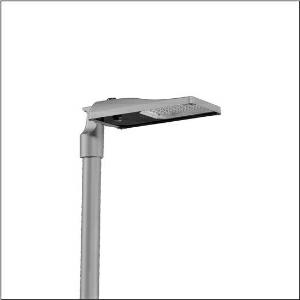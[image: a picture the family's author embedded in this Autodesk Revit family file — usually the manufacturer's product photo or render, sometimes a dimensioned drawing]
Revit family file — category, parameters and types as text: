
# Revit family: streetlight_sl_31_mini___st1_0a_5xh2d31t08ja_3c6a
name_source: partatom
category: Lighting Fixtures
units: mm (PartAtom-declared; Revit-internal decimal feet)

## family parameters
Cut with Voids When Loaded = No
Host = Face
Light Source = No
Part Type = Normal
Room Calculation Point = No
Round Connector Dimension = Use Diameter
Shared = No

## types (1)
- --- (1 x LED, 12270 lm, 82.5 W, 3000K)
    Apparent Load = 83 VA
    CIE Flux Codes = 40 73 97 100 100
    Color Rendering = 70
    Color Temperature = 3000K
    Default Elevation = 1800 mm
    Description = Streetlight SL 31 mini D4i, Desk-Remote mast luminaire for post-top, side-entry; light control with lens of PMMA; light distribution: ST1.0a, direct asymmetric distribution, for standard-compliant lighting for roads and squares; LED: luminous flux: 12.270lm, light colour: 730, colour temperature: 3000K; luminous efficacy: 148,7lm/W; control: pre-setting: logarithmic dimming characteristic, flexible luminous flux parameterisation, time-dependent luminous flux control, constant luminous flux control, power reduction, intelligent temperature release in ECG and LED module, overheat protection; luminaire housing, of diecast aluminium, Siteco® metallic grey (DB 702S), corrosivity category C5 high according to DIN EN ISO 12944; cover of toughened safety glass, transparent, mast flange of diecast aluminium, Siteco® metallic grey (DB 702S), spigot size: 76/60mm, mast flange included unmounted; with cable H07RN-F 2x 1.5mm², cable length: 10,5m, connection cable pre-assembled; mains connection: 220..240V, AC, 50/60Hz; power consumption (at start of service life): 82,5W / (at end of service life): 90,1W / (with reduced operation 50%): 36,8W; protection rating (complete): IP66; insulation class (complete): insulation class II (safety insulation); impact resistance: IK09; certification: CE, ENEC, ENEC+, VDE, UKCA, ZD4i; permissible operating ambient temperature for outdoor applications: -40..+50°C; packaging unit: 1 piece

Light Distribution: ST1.0a
    Height = 76 mm
    Lamp = 1 x LED
    Lamp Light Flux = 12270 lm
    Lamp Power = 82.5 W
    Lamp count = 1
    Length = 547 mm
    Luminous efficacy = 149 lm/W
    Manufacturer = Siteco
    ModVariant = No
    Model = 5XH2D31T08JA
    Number of Poles = 1
    OnlyDefault = Yes
    Power Factor = 1
    Product Name = Streetlight SL 31 mini | ST1.0a
    Product group = mast luminaire | pylon top
    ProductGroupID = 6100
    Protection Class = Protection class II
    Protection Degree = IP 66
    RLX_Detail_Level = 1
    RLX_Emergency_Light_Flux = 0 lm
    RLX_Emergency_Type = 0
    RLX_Emergency_Type_DB = No
    RlxData = <blob elided: 39913 chars, md5=c4d5aa8d>
    Socket = socket
    Standby Power = 0 W
    System Light Flux = 12270 lm
    System Power = 83 W
    Type Comments = factory setting: luminous flux: 100 % | dim-lin: 254 | 870 mA
    Type Image = l_1300332.jpg
    URL = http://relux.com
    VarID = @adj_050806
    Voltage = 0 V
    Weight = 0.00 kg
    Width = 265 mm

## geometry (parser evidence)
native form markers: Blend x4, Sweep x10
no freeform markers — native parametric forms only
